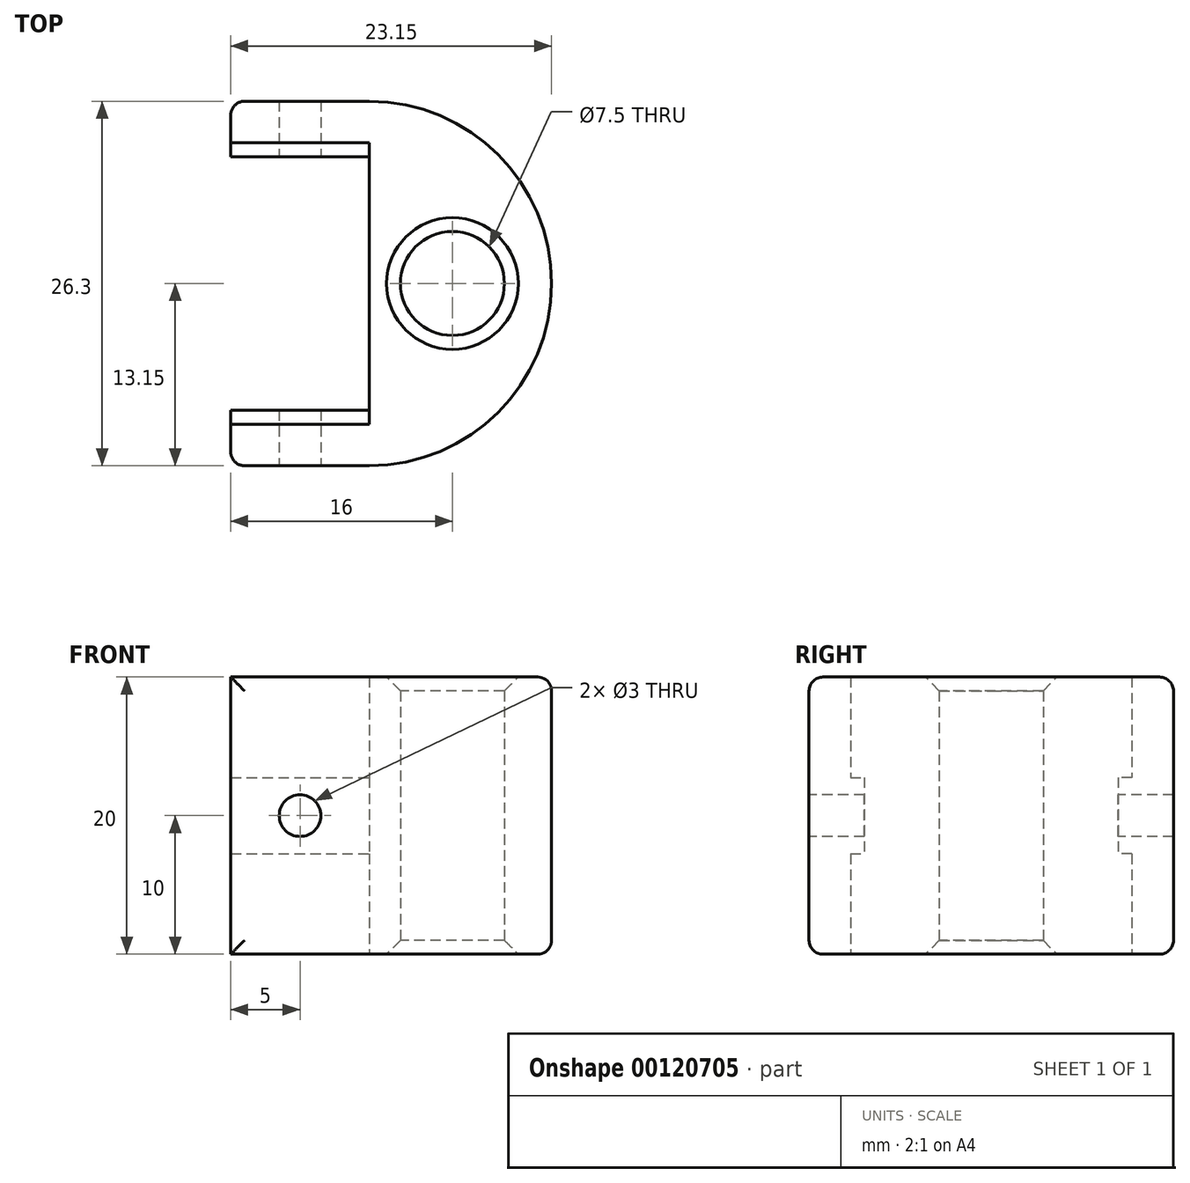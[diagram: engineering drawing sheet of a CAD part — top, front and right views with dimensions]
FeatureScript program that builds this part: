
annotation { "Feature Type Name" : "Feature", "Feature Type Description" : "" }
export const myFeature = defineFeature(function(context is Context, id is Id, definition is map)
    precondition{}
    {
        {
            var Q0;
            Q0=qCreatedBy(makeId("Top.planeOp"),FACE);
            var sketch = newSketch(context, id + "F0", { "sketchPlane" : qUnion([Q0])});
            skLineSegment(sketch, "E0", {"start": v(0, 0) * mm, "end": v(0, 3) * mm});
            skLineSegment(sketch, "E1", {"start": v(0, 3) * mm, "end": v(10, 3) * mm});
            skLineSegment(sketch, "E2", {"start": v(10, 3) * mm, "end": v(10, 23.3) * mm});
            skLineSegment(sketch, "E3", {"start": v(10, 23.3) * mm, "end": v(0, 23.3) * mm});
            skLineSegment(sketch, "E4", {"start": v(0, 23.3) * mm, "end": v(0, 26.3) * mm});
            skLineSegment(sketch, "E5", {"start": v(0, 26.3) * mm, "end": v(10, 26.3) * mm});
            skLineSegment(sketch, "E6", {"start": v(0, 0) * mm, "end": v(10, 0) * mm});
            skArc(sketch, "E7", {"start": v(10, 26.3) * mm, "mid": v(23.15, 13.15) * mm, "end": v(10, 0) * mm});
            skCircle(sketch, "E8", {"center": v(16, 13.15) * mm, "radius": 3.75 * mm});
            skSolve(sketch);
        }
        {
            var Q0;
            Q0=makeQuery(id+"F0.imprint","IMPRINT",FACE,{"disambiguationData":[TD([[makeQuery(id+"F0.imprint","IMPRINT",EDGE,{"derivedFrom":sQuery(id+"F0.wireOp",EDGE,"E0")}),-1.0]])]});
            extrude(context, id + "F1", {"entities" : qUnion([Q0]), "depth" : 20 * mm});
        }
        {
            var Q0;
            Q0=makeQuery(id+"F1.opExtrude","SWEPT_FACE",FACE,{"disambiguationData":[OSD([sQuery(id+"F0.wireOp",EDGE,"E2")])]});
            var sketch = newSketch(context, id + "F2", { "sketchPlane" : qUnion([Q0])});
            skLineSegment(sketch, "E9.bottom", {"start": v(-23.3, 12.75) * mm, "end": v(-22.3, 12.75) * mm});
            skLineSegment(sketch, "E9.top", {"start": v(-23.3, 7.25) * mm, "end": v(-22.3, 7.25) * mm});
            skLineSegment(sketch, "E9.left", {"start": v(-23.3, 12.75) * mm, "end": v(-23.3, 7.25) * mm});
            skLineSegment(sketch, "E9.right", {"start": v(-22.3, 12.75) * mm, "end": v(-22.3, 7.25) * mm});
            skLineSegment(sketch, "E10.bottom", {"start": v(-3, 12.75) * mm, "end": v(-4, 12.75) * mm});
            skLineSegment(sketch, "E10.top", {"start": v(-3, 7.25) * mm, "end": v(-4, 7.25) * mm});
            skLineSegment(sketch, "E10.left", {"start": v(-3, 12.75) * mm, "end": v(-3, 7.25) * mm});
            skLineSegment(sketch, "E10.right", {"start": v(-4, 12.75) * mm, "end": v(-4, 7.25) * mm});
            skSolve(sketch);
        }
        {
            var Q0;
            Q0 = qSketchRegion(id + "F2", true);
            var Q1;
            Q1=makeQuery(id+"F1.opExtrude","SWEPT_FACE",FACE,{"disambiguationData":[OSD([sQuery(id+"F0.wireOp",EDGE,"E4")])]});
            extrude(context, id + "F3", {"entities" : qUnion([Q0]), "operationType" : NewBodyOperationType.ADD, "endBound" : BoundingType.UP_TO_SURFACE, "endBoundEntityFace" : qUnion([Q1]), "depth" : 25 * mm});
        }
        {
            var Q0;
            Q0=makeQuery(id+"F1.opExtrude","SWEPT_FACE",FACE,{"disambiguationData":[OSD([sQuery(id+"F0.wireOp",EDGE,"E6")])]});
            var sketch = newSketch(context, id + "F4", { "sketchPlane" : qUnion([Q0])});
            skCircle(sketch, "E11", {"center": v(5, 10) * mm, "radius": 1.5 * mm});
            skPoint(sketch, "E11.centerSnap0", {"position": v(5, 0) * mm});
            skPoint(sketch, "E11.centerSnap1", {"position": v(0, 10) * mm});
            skSolve(sketch);
        }
        {
            var Q0;
            Q0 = qSketchRegion(id + "F4", true);
            extrude(context, id + "F5", {"entities" : qUnion([Q0]), "operationType" : NewBodyOperationType.REMOVE, "endBound" : BoundingType.THROUGH_ALL, "oppositeDirection" : true, "depth" : 25 * mm});
        }
        {
            var Q0;
            Q0=makeQuery(id+"F1.opExtrude","CAP_EDGE",EDGE,{"disambiguationData":[OSD([sQuery(id+"F0.wireOp",EDGE,"E8")])],"isStart":false});
            var Q1;
            Q1=makeQuery(id+"F1.opExtrude","CAP_EDGE",EDGE,{"disambiguationData":[OSD([sQuery(id+"F0.wireOp",EDGE,"E8")])],"isStart":true});
            chamfer(context, id + "F6", {"entities" : qUnion([Q0, Q1]), "width" : 1 * mm, "tangentPropagation" : true});
        }
        {
            var Q0;
            Q0=makeQuery(id+"F1.opExtrude","CAP_EDGE",EDGE,{"disambiguationData":[OSD([sQuery(id+"F0.wireOp",EDGE,"E7")])],"isStart":false});
            var Q1;
            Q1=makeQuery(id+"F1.opExtrude","CAP_EDGE",EDGE,{"disambiguationData":[OSD([sQuery(id+"F0.wireOp",EDGE,"E7")])],"isStart":true});
            var Q2;
            Q2=makeQuery(id+"F1.opExtrude","SWEPT_EDGE",EDGE,{"disambiguationData":[OSD([sQuery(id+"F0.wireOp",EDGE,"E0"),sQuery(id+"F0.wireOp",EDGE,"E6")])]});
            var Q3;
            Q3=makeQuery(id+"F1.opExtrude","SWEPT_EDGE",EDGE,{"disambiguationData":[OSD([sQuery(id+"F0.wireOp",EDGE,"E4"),sQuery(id+"F0.wireOp",EDGE,"E5")])]});
            fillet(context, id + "F7", {"entities" : qUnion([Q0, Q1, Q2, Q3]), "radius" : 1 * mm, "tangentPropagation" : true, "allowEdgeOverflow" : false});
        }
    });
